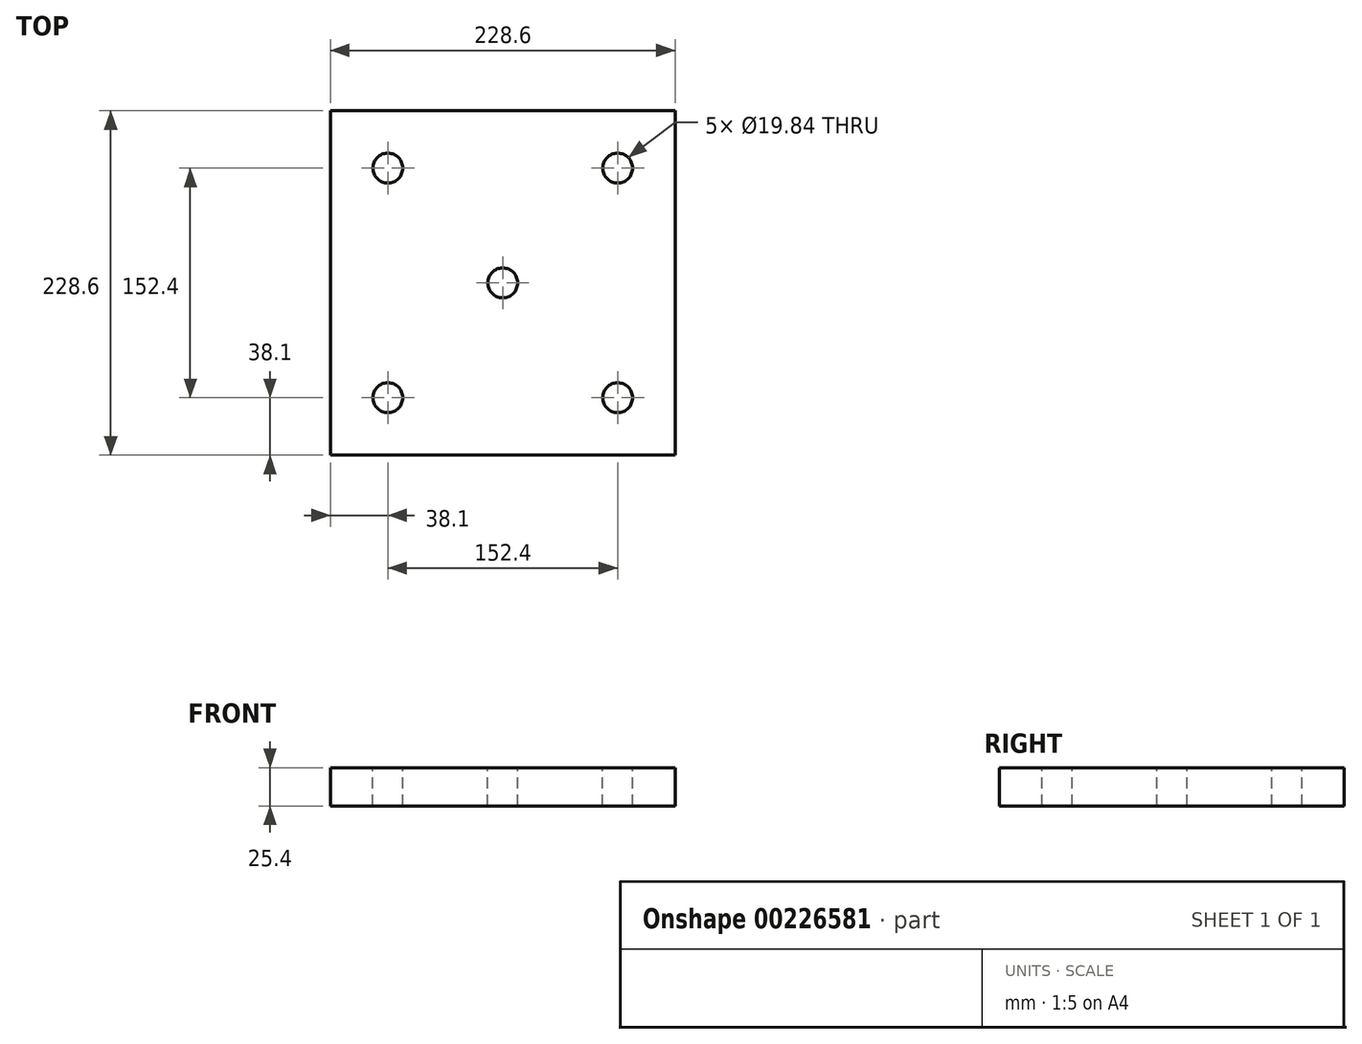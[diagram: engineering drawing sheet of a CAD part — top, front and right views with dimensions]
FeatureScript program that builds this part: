
annotation { "Feature Type Name" : "Feature", "Feature Type Description" : "" }
export const myFeature = defineFeature(function(context is Context, id is Id, definition is map)
    precondition{}
    {
        {
            var Q0;
            Q0=qCreatedBy(makeId("Top.planeOp"),FACE);
            var sketch = newSketch(context, id + "F0", { "sketchPlane" : qUnion([Q0])});
            skLineSegment(sketch, "E0.bottom", {"start": v(114.3, 114.3) * mm, "end": v(-114.3, 114.3) * mm});
            skLineSegment(sketch, "E0.top", {"start": v(114.3, -114.3) * mm, "end": v(-114.3, -114.3) * mm});
            skLineSegment(sketch, "E0.left", {"start": v(114.3, 114.3) * mm, "end": v(114.3, -114.3) * mm});
            skLineSegment(sketch, "E0.right", {"start": v(-114.3, 114.3) * mm, "end": v(-114.3, -114.3) * mm});
            skPoint(sketch, "E0.middle", {"position": v(0, 0) * mm});
            skSolve(sketch);
        }
        {
            var Q0;
            Q0=qSketchRegion(id+"F0",true);
            extrude(context, id + "F1", {"entities" : qUnion([Q0]), "oppositeDirection" : true, "depth" : 25.4 * mm, "symmetric" : true});
        }
        {
            var Q0;
            Q0=makeQuery(id+"F1.opExtrude","CAP_FACE",FACE,{"disambiguationData":[OSD([sQuery(id+"F0.wireOp",EDGE,"E0.bottom"),sQuery(id+"F0.wireOp",EDGE,"E0.top"),sQuery(id+"F0.wireOp",EDGE,"E0.left"),sQuery(id+"F0.wireOp",EDGE,"E0.right")])],"isStart":true});
            var sketch = newSketch(context, id + "F2", { "sketchPlane" : qUnion([Q0])});
            skLineSegment(sketch, "E1.bottom", {"start": v(76.2, 76.2) * mm, "end": v(-76.2, 76.2) * mm});
            skLineSegment(sketch, "E1.top", {"start": v(76.2, -76.2) * mm, "end": v(-76.2, -76.2) * mm});
            skLineSegment(sketch, "E1.left", {"start": v(76.2, 76.2) * mm, "end": v(76.2, -76.2) * mm});
            skLineSegment(sketch, "E1.right", {"start": v(-76.2, 76.2) * mm, "end": v(-76.2, -76.2) * mm});
            skPoint(sketch, "E1.middle", {"position": v(0, 0) * mm});
            skSolve(sketch);
        }
        {
            var Q0;
            Q0=sQuery(id+"F2.wireOp",VERTEX,"E1.right.start");
            var Q1;
            Q1=sQuery(id+"F2.wireOp",VERTEX,"E1.left.start");
            var Q2;
            Q2=sQuery(id+"F2.wireOp",VERTEX,"E1.top.end");
            var Q3;
            Q3=sQuery(id+"F2.wireOp",VERTEX,"E1.left.end");
            var Q4;
            Q4=makeQuery(id+"F1.opExtrude","SWEPT_BODY",BODY,{"disambiguationData":[OSD([sQuery(id+"F0.wireOp",EDGE,"E0.bottom"),sQuery(id+"F0.wireOp",EDGE,"E0.top"),sQuery(id+"F0.wireOp",EDGE,"E0.left"),sQuery(id+"F0.wireOp",EDGE,"E0.right")])]});
            hole(context, id + "F3", {"style" : HoleStyle.SIMPLE, "endStyle" : HoleEndStyle.THROUGH, "standardTappedOrClearance" : lookupTablePath({ "standard" : "ANSI", "fit" : "Normal (ASME)", "size" : "3/4", "type" : "Clearance" }), "standardBlindInLast" : lookupTablePath({ "fit" : "Free", "standard" : "ANSI", "size" : "3/4", "type" : "Clearance" }), "holeDiameter" : 19.84 * mm, "locations" : qUnion([Q0, Q1, Q2, Q3]), "scope" : qUnion([Q4]), "isTappedThrough" : true});
        }
        {
            var Q0;
            Q0=sQuery(id+"F2.wireOp",VERTEX,"E1.middle");
            var Q1;
            Q1=makeQuery(id+"F1.opExtrude","SWEPT_BODY",BODY,{"disambiguationData":[OSD([sQuery(id+"F0.wireOp",EDGE,"E0.bottom"),sQuery(id+"F0.wireOp",EDGE,"E0.top"),sQuery(id+"F0.wireOp",EDGE,"E0.left"),sQuery(id+"F0.wireOp",EDGE,"E0.right")])]});
            hole(context, id + "F4", {"style" : HoleStyle.SIMPLE, "endStyle" : HoleEndStyle.THROUGH, "standardTappedOrClearance" : lookupTablePath({ "standard" : "ANSI", "fit" : "Normal (ASME)", "size" : "3/4", "type" : "Clearance" }), "standardBlindInLast" : lookupTablePath({ "fit" : "Free", "standard" : "ANSI", "size" : "3/4", "type" : "Clearance" }), "holeDiameter" : 19.84 * mm, "locations" : qUnion([Q0]), "scope" : qUnion([Q1]), "isTappedThrough" : true});
        }
    });
